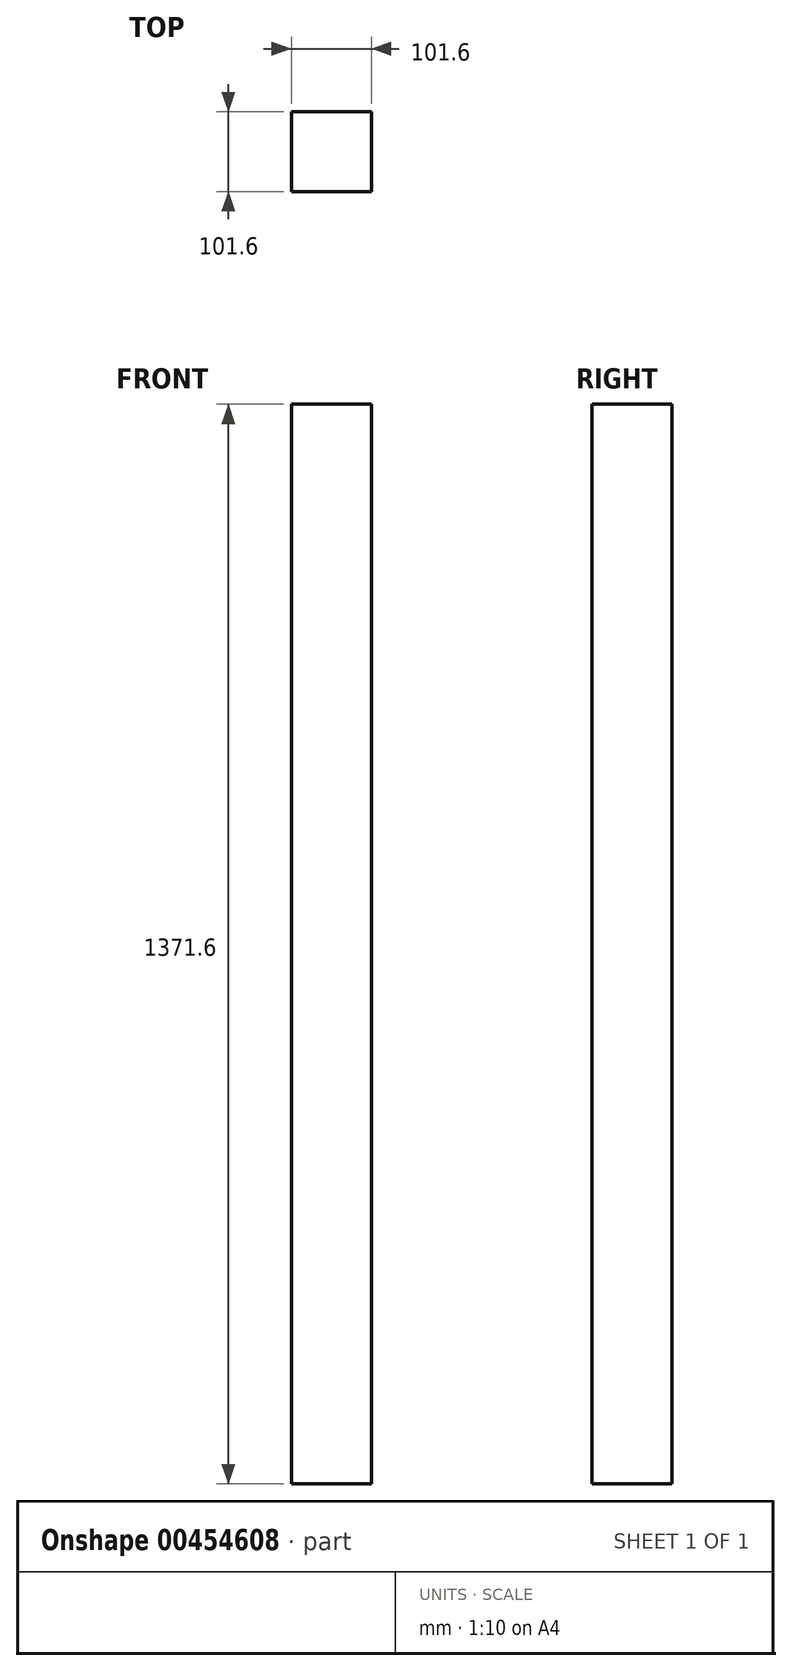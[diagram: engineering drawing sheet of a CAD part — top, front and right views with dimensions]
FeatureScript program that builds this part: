
annotation { "Feature Type Name" : "Feature", "Feature Type Description" : "" }
export const myFeature = defineFeature(function(context is Context, id is Id, definition is map)
    precondition{}
    {
        {
            var Q0;
            Q0=qCreatedBy(makeId("Top.planeOp"),FACE);
            var sketch = newSketch(context, id + "F0", { "sketchPlane" : qUnion([Q0])});
            skLineSegment(sketch, "E0.bottom", {"start": v(50.8, 50.8) * mm, "end": v(-50.8, 50.8) * mm});
            skLineSegment(sketch, "E0.top", {"start": v(50.8, -50.8) * mm, "end": v(-50.8, -50.8) * mm});
            skLineSegment(sketch, "E0.left", {"start": v(50.8, 50.8) * mm, "end": v(50.8, -50.8) * mm});
            skLineSegment(sketch, "E0.right", {"start": v(-50.8, 50.8) * mm, "end": v(-50.8, -50.8) * mm});
            skPoint(sketch, "E0.middle", {"position": v(0, 0) * mm});
            skSolve(sketch);
        }
        {
            var Q0;
            Q0=makeQuery(id+"F0.imprint","IMPRINT",FACE,{"disambiguationData":[TD([[makeQuery(id+"F0.imprint","IMPRINT",EDGE,{"derivedFrom":sQuery(id+"F0.wireOp",EDGE,"E0.bottom")}),1.0]])]});
            extrude(context, id + "F1", {"entities" : qUnion([Q0]), "depth" : 1371.6 * mm});
        }
    });
